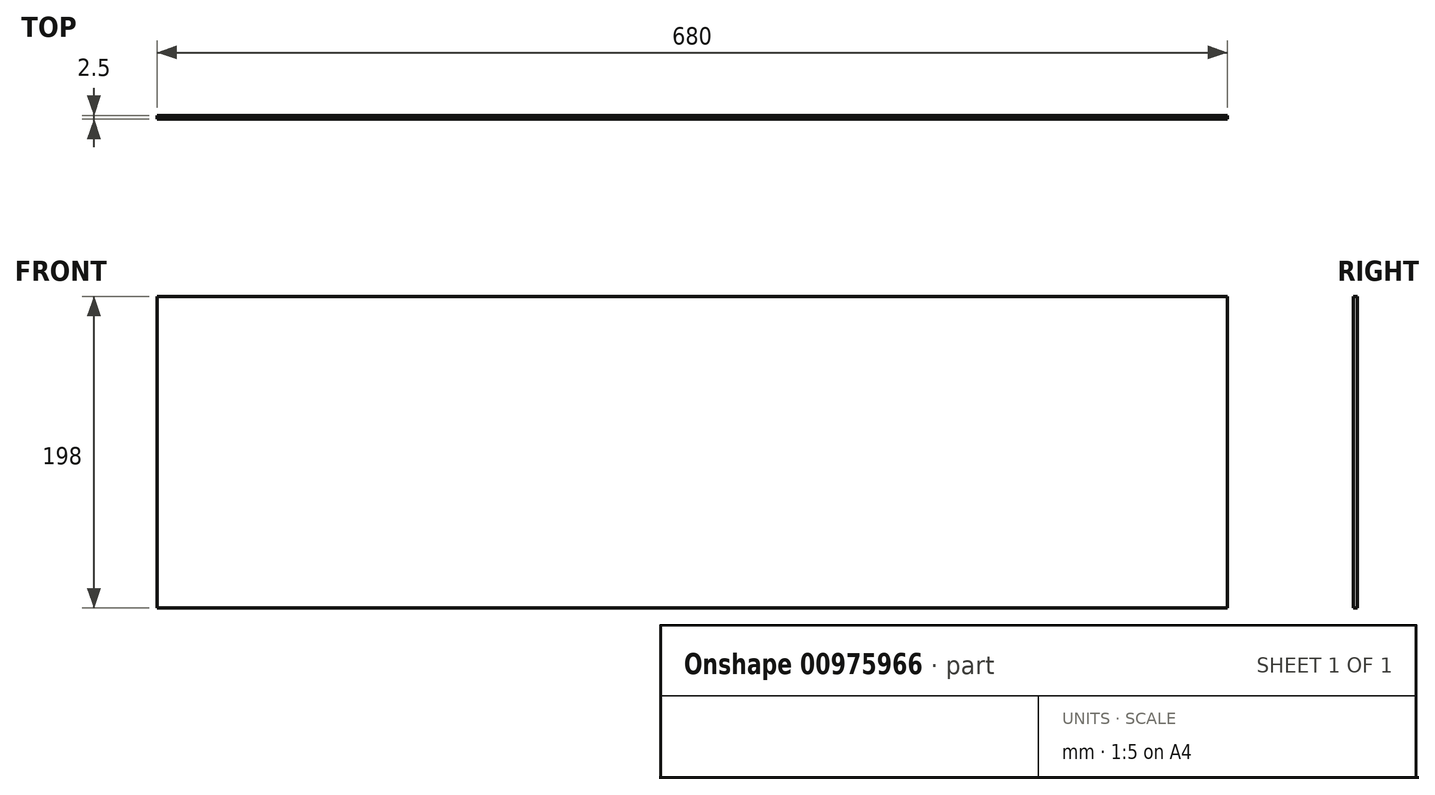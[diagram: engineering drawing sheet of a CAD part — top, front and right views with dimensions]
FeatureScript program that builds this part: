
annotation { "Feature Type Name" : "Feature", "Feature Type Description" : "" }
export const myFeature = defineFeature(function(context is Context, id is Id, definition is map)
    precondition{}
    {
        {
            var Q0;
            Q0=qCreatedBy(makeId("Front.planeOp"),FACE);
            var sketch = newSketch(context, id + "F0", { "sketchPlane" : qUnion([Q0])});
            skLineSegment(sketch, "E0.bottom", {"start": v(340, -99) * mm, "end": v(-340, -99) * mm});
            skLineSegment(sketch, "E0.top", {"start": v(340, 99) * mm, "end": v(-340, 99) * mm});
            skLineSegment(sketch, "E0.left", {"start": v(340, -99) * mm, "end": v(340, 99) * mm});
            skLineSegment(sketch, "E0.right", {"start": v(-340, -99) * mm, "end": v(-340, 99) * mm});
            skPoint(sketch, "E0.middle", {"position": v(0, 0) * mm});
            skSolve(sketch);
        }
        {
            var Q0;
            Q0=makeQuery(id+"F0.imprint","IMPRINT",FACE,{"disambiguationData":[TD([[makeQuery(id+"F0.imprint","IMPRINT",EDGE,{"derivedFrom":sQuery(id+"F0.wireOp",EDGE,"E0.bottom")}),-1.0]])]});
            extrude(context, id + "F1", {"entities" : qUnion([Q0]), "depth" : 2.5 * mm, "offsetDistance" : 25 * mm});
        }
    });
